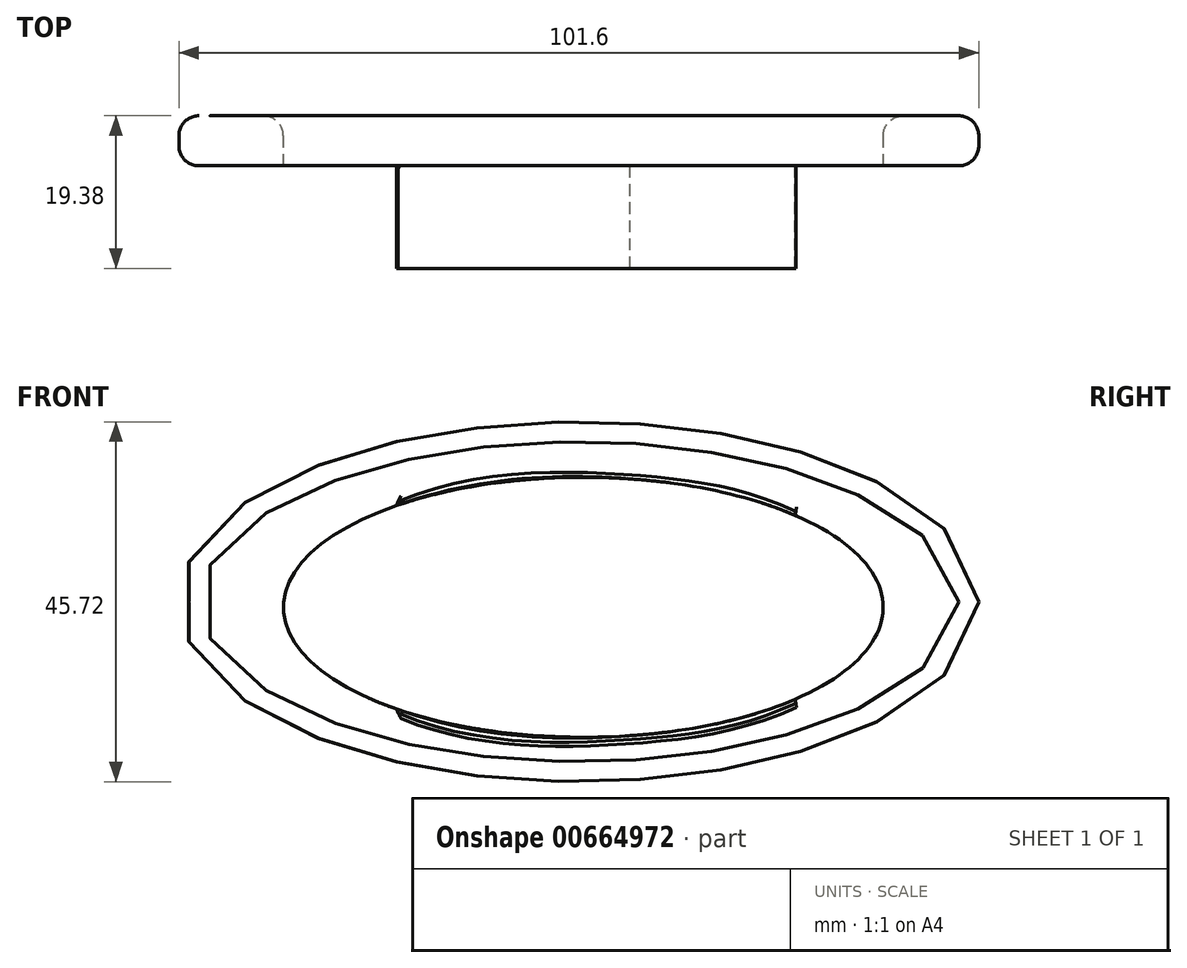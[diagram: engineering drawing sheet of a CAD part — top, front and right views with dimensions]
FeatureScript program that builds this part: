
annotation { "Feature Type Name" : "Feature", "Feature Type Description" : "" }
export const myFeature = defineFeature(function(context is Context, id is Id, definition is map)
    precondition{}
    {
        {
            var Q0;
            Q0=qCreatedBy(makeId("Front.planeOp"),FACE);
            var sketch = newSketch(context, id + "F0", { "sketchPlane" : qUnion([Q0])});
            skEllipse(sketch, "E0", {"center": v(0, 0) * mm, "majorRadius": 16.51 * mm, "minorRadius": 38.1 * mm, "majorAxis": v(0, -1)});
            skSolve(sketch);
        }
        {
            var Q0;
            Q0=qCreatedBy(makeId("Front.planeOp"),FACE);
            var sketch = newSketch(context, id + "F1", { "sketchPlane" : qUnion([Q0])});
            skEllipse(sketch, "E1", {"center": v(-0.56, 0.7) * mm, "majorRadius": 22.86 * mm, "minorRadius": 50.8 * mm, "majorAxis": v(0, -1)});
            skSolve(sketch);
        }
        {
            var Q0;
            Q0=makeQuery(id+"F1.imprint","IMPRINT",FACE,{"disambiguationData":[TD([[makeQuery(id+"F1.imprint","IMPRINT",EDGE,{"derivedFrom":sQuery(id+"F1.wireOp",EDGE,"E1")}),1.0]])]});
            extrude(context, id + "F2", {"entities" : qUnion([Q0]), "depth" : 6.35 * mm, "offsetDistance" : 25.4 * mm});
        }
        {
            var Q0;
            Q0=makeQuery(id+"F0.imprint","IMPRINT",FACE,{"disambiguationData":[TD([[makeQuery(id+"F0.imprint","IMPRINT",EDGE,{"derivedFrom":sQuery(id+"F0.wireOp",EDGE,"E0")}),1.0]])]});
            extrude(context, id + "F3", {"entities" : qUnion([Q0]), "operationType" : NewBodyOperationType.REMOVE, "endBound" : BoundingType.SYMMETRIC, "oppositeDirection" : true, "depth" : 25.4 * mm, "offsetDistance" : 25.4 * mm});
        }
        {
            var Q0;
            Q0=makeQuery(id+"F2.opExtrude","CAP_FACE",FACE,{"disambiguationData":[OSD([sQuery(id+"F1.wireOp",EDGE,"E1")])],"isStart":false});
            var sketch = newSketch(context, id + "F4", { "sketchPlane" : qUnion([Q0])});
            skFitSpline(sketch, "E2", {"points": [v(26.9, -11.7) * mm, v(5.97, -16.3) * mm, v(-23.74, -12.91) * mm], "startDerivative": vector(-46.04, -15.67) * mm, "endDerivative": vector(-55.78, 20.39) * mm});
            skFitSpline(sketch, "E3", {"points": [v(27, -12.2) * mm, v(6.05, -16.8) * mm, v(-23.5, -13.42) * mm], "startDerivative": vector(-45.83, -20.82) * mm, "endDerivative": vector(-53.1, 23.27) * mm});
            skLineSegment(sketch, "E4", {"start": v(27, -12.2) * mm, "end": v(26.9, -11.7) * mm});
            skLineSegment(sketch, "E5", {"start": v(-23.5, -13.42) * mm, "end": v(-23.74, -12.91) * mm});
            skFitSpline(sketch, "E6.MirrorCS", {"points": [v(26.9, 11.7) * mm, v(5.97, 16.3) * mm, v(-23.74, 12.91) * mm], "startDerivative": vector(-46.04, 15.67) * mm, "endDerivative": vector(-55.78, -20.39) * mm});
            skFitSpline(sketch, "E7.MirrorCS", {"points": [v(27, 12.2) * mm, v(6.05, 16.8) * mm, v(-23.5, 13.42) * mm], "startDerivative": vector(-45.83, 20.82) * mm, "endDerivative": vector(-53.1, -23.27) * mm});
            skLineSegment(sketch, "E8.MirrorCS", {"start": v(27, 12.2) * mm, "end": v(26.9, 11.7) * mm});
            skLineSegment(sketch, "E9.MirrorCS", {"start": v(-23.5, 13.42) * mm, "end": v(-23.74, 12.91) * mm});
            skSolve(sketch);
        }
        {
            var Q0;
            {var subQ0=sQuery(id+"F4.wireOp",EDGE,"E4");Q0=makeQuery(id+"F4.imprint","IMPRINT",FACE,{"disambiguationData":[TD([[makeQuery(id+"F4.imprint","IMPRINT",EDGE,{"derivedFrom":subQ0}),1.0]])]});}
            var Q1;
            Q1=makeQuery(id+"F4.imprint","IMPRINT",FACE,{"disambiguationData":[TD([[makeQuery(id+"F4.imprint","IMPRINT",EDGE,{"derivedFrom":sQuery(id+"F4.wireOp",EDGE,"E7.MirrorCS")}),1.0]])]});
            extrude(context, id + "F5", {"entities" : qUnion([Q0, Q1]), "operationType" : NewBodyOperationType.ADD, "depth" : 13.03 * mm, "offsetDistance" : 25.4 * mm});
        }
        {
            var Q0;
            Q0=makeQuery(id+"F5.opExtrude","CAP_EDGE",EDGE,{"disambiguationData":[OSD([sQuery(id+"F4.wireOp",EDGE,"E3")])],"isStart":true});
            var Q1;
            Q1=makeQuery(id+"F5.opExtrude","CAP_EDGE",EDGE,{"disambiguationData":[OSD([sQuery(id+"F4.wireOp",EDGE,"E7.MirrorCS")])],"isStart":true});
            fillet(context, id + "F6", {"entities" : qUnion([Q0, Q1]), "radius" : 0.5 * mm, "tangentPropagation" : true, "allowEdgeOverflow" : false});
        }
        {
            var Q0;
            Q0=makeQuery(id+"F2.opExtrude","CAP_EDGE",EDGE,{"disambiguationData":[OSD([sQuery(id+"F1.wireOp",EDGE,"E1")])],"isStart":false});
            var Q1;
            Q1=makeQuery(id+"F2.opExtrude","CAP_EDGE",EDGE,{"disambiguationData":[OSD([sQuery(id+"F1.wireOp",EDGE,"E1")])],"isStart":true});
            var Q2;
            Q2=makeQuery(id+"F3.boolean.opBoolean","INTERSECT",EDGE,{"derivedFrom":[makeQuery(id+"F2.opExtrude","CAP_FACE",FACE,{"disambiguationData":[OSD([sQuery(id+"F1.wireOp",EDGE,"E1")])],"isStart":true}),makeQuery(id+"F3.opExtrude","SWEPT_FACE",FACE,{"disambiguationData":[OSD([sQuery(id+"F0.wireOp",EDGE,"E0")])]})]});
            fillet(context, id + "F7", {"entities" : qUnion([Q0, Q1, Q2]), "radius" : 2.54 * mm, "tangentPropagation" : true, "allowEdgeOverflow" : false});
        }
    });
